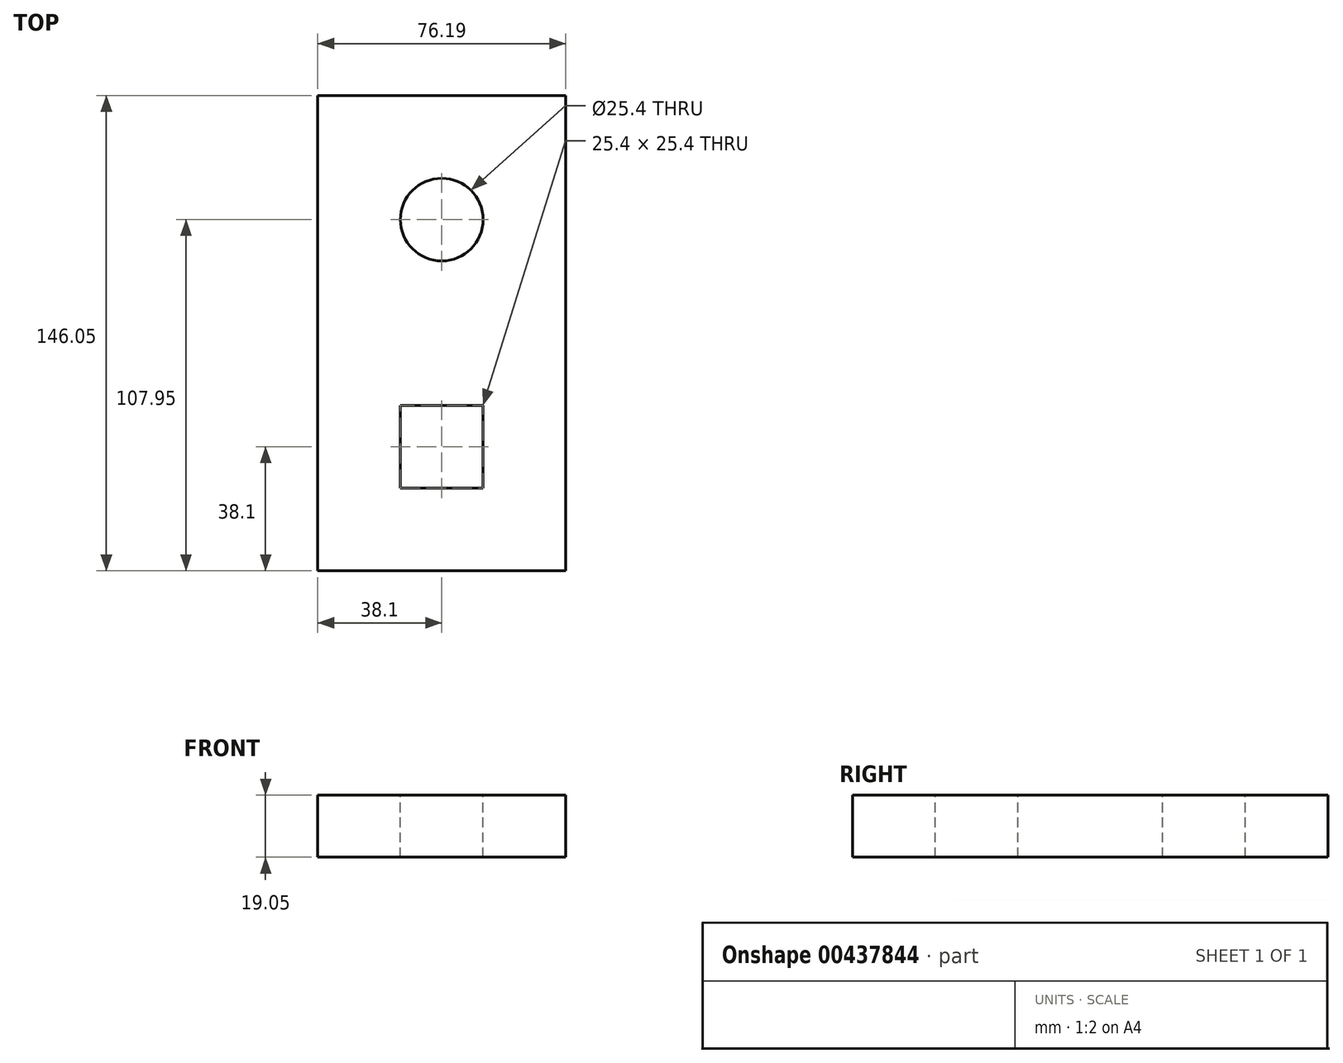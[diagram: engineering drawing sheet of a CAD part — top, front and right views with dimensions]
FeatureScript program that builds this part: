
annotation { "Feature Type Name" : "Feature", "Feature Type Description" : "" }
export const myFeature = defineFeature(function(context is Context, id is Id, definition is map)
    precondition{}
    {
        {
            var Q0;
            Q0=qCreatedBy(makeId("Front.planeOp"),FACE);
            var sketch = newSketch(context, id + "F0", { "sketchPlane" : qUnion([Q0])});
            skLineSegment(sketch, "E0", {"start": v(0, 0) * mm, "end": v(76.2, 0) * mm});
            skLineSegment(sketch, "E1", {"start": v(76.2, 0) * mm, "end": v(76.2, 19.05) * mm});
            skLineSegment(sketch, "E2", {"start": v(76.2, 19.05) * mm, "end": v(0, 19.05) * mm});
            skLineSegment(sketch, "E3", {"start": v(0, 19.05) * mm, "end": v(0, 0) * mm});
            skSolve(sketch);
        }
        {
            var Q0;
            Q0 = qSketchRegion(id + "F0", true);
            extrude(context, id + "F1", {"entities" : qUnion([Q0]), "depth" : 146.05 * mm});
        }
        {
            var Q0;
            Q0=makeQuery(id+"F1.opExtrude","SWEPT_FACE",FACE,{"disambiguationData":[OSD([sQuery(id+"F0.wireOp",EDGE,"E2")])]});
            var sketch = newSketch(context, id + "F2", { "sketchPlane" : qUnion([Q0])});
            skLineSegment(sketch, "E4.bottom", {"start": v(25.4, -120.65) * mm, "end": v(50.8, -120.65) * mm});
            skLineSegment(sketch, "E4.top", {"start": v(25.4, -95.25) * mm, "end": v(50.8, -95.25) * mm});
            skLineSegment(sketch, "E4.left", {"start": v(25.4, -120.65) * mm, "end": v(25.4, -95.25) * mm});
            skLineSegment(sketch, "E4.right", {"start": v(50.8, -120.65) * mm, "end": v(50.8, -95.25) * mm});
            skCircle(sketch, "E5", {"center": v(38.1, -38.1) * mm, "radius": 12.7 * mm});
            skSolve(sketch);
        }
        {
            var Q0;
            Q0=makeQuery(id+"F2.imprint","IMPRINT",FACE,{"disambiguationData":[TD([[makeQuery(id+"F2.imprint","IMPRINT",EDGE,{"derivedFrom":sQuery(id+"F2.wireOp",EDGE,"E4.bottom")}),1.0]])]});
            extrude(context, id + "F3", {"entities" : qUnion([Q0]), "operationType" : NewBodyOperationType.REMOVE, "oppositeDirection" : true, "depth" : 25.4 * mm});
        }
        {
            var Q0;
            Q0=makeQuery(id+"F1.opExtrude","SWEPT_FACE",FACE,{"disambiguationData":[OSD([sQuery(id+"F0.wireOp",EDGE,"E2")])]});
            var sketch = newSketch(context, id + "F4", { "sketchPlane" : qUnion([Q0])});
            skCircle(sketch, "E6", {"center": v(38.1, -38.1) * mm, "radius": 12.7 * mm});
            skSolve(sketch);
        }
        {
            var Q0;
            Q0 = qSketchRegion(id + "F4", true);
            extrude(context, id + "F5", {"entities" : qUnion([Q0]), "operationType" : NewBodyOperationType.REMOVE, "oppositeDirection" : true, "depth" : 25.4 * mm});
        }
    });
